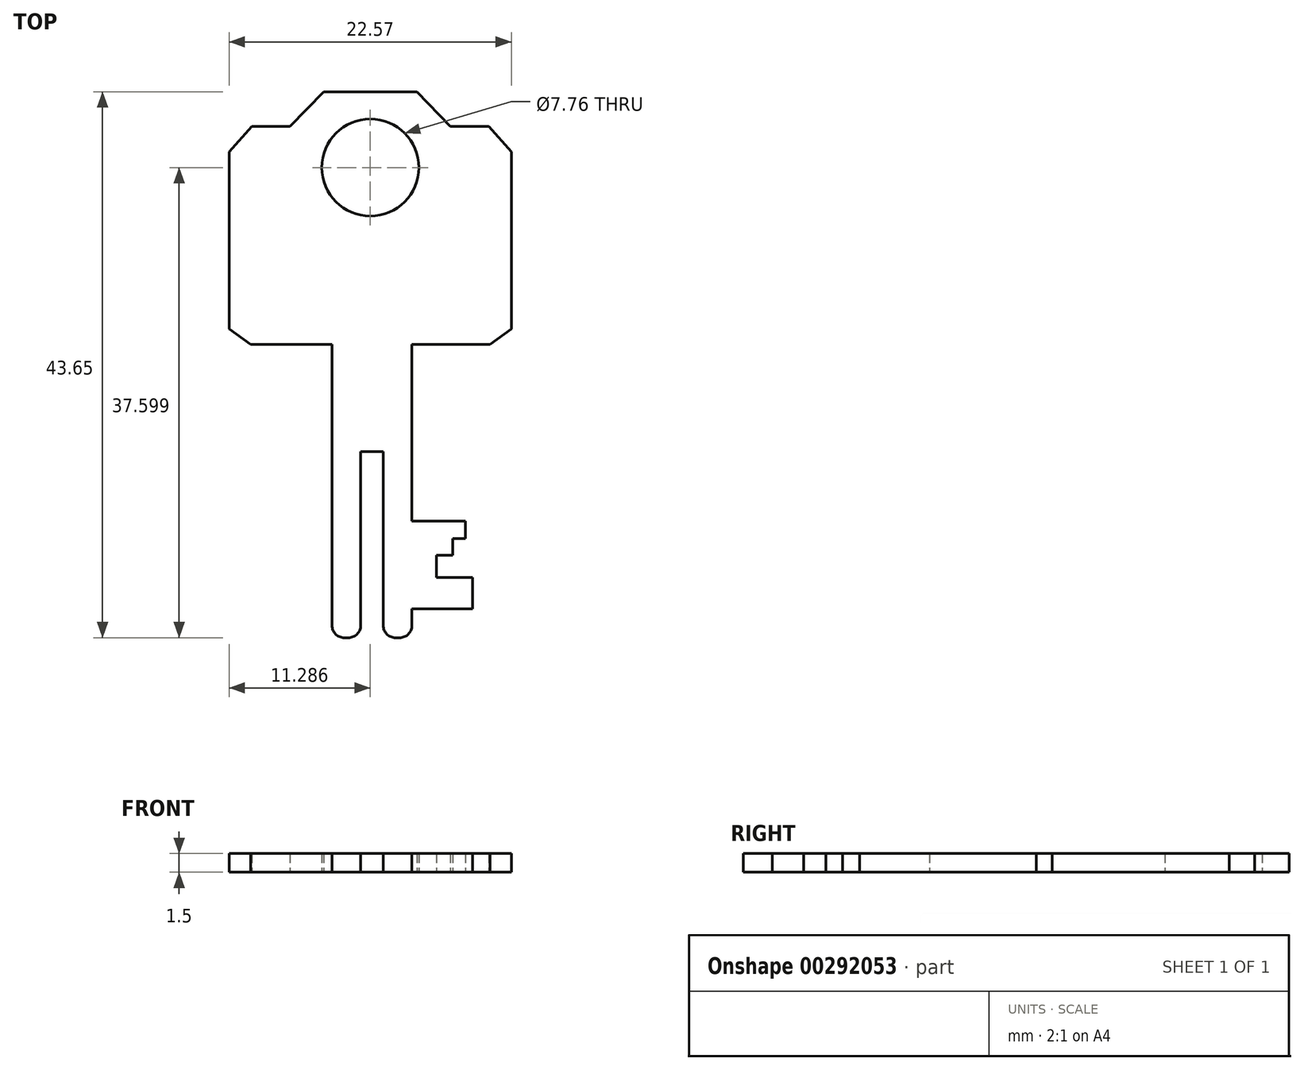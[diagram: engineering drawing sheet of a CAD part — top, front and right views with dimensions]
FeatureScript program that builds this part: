
annotation { "Feature Type Name" : "Feature", "Feature Type Description" : "" }
export const myFeature = defineFeature(function(context is Context, id is Id, definition is map)
    precondition{}
    {
        {
            var Q0;
            Q0=qCreatedBy(makeId("Top.planeOp"),FACE);
            var sketch = newSketch(context, id + "F0", { "sketchPlane" : qUnion([Q0])});
            skLineSegment(sketch, "E0", {"start": v(-40.44, -25.58) * mm, "end": v(-40.44, -51.76) * mm});
            skLineSegment(sketch, "E1", {"start": v(-40.44, -51.76) * mm, "end": v(-38.14, -51.76) * mm});
            skLineSegment(sketch, "E2", {"start": v(-38.14, -51.76) * mm, "end": v(-38.14, -36.87) * mm});
            skLineSegment(sketch, "E3", {"start": v(-38.14, -36.87) * mm, "end": v(-36.34, -36.87) * mm});
            skLineSegment(sketch, "E4", {"start": v(-36.34, -36.87) * mm, "end": v(-36.34, -51.76) * mm});
            skLineSegment(sketch, "E5", {"start": v(-36.34, -51.76) * mm, "end": v(-34.04, -51.76) * mm});
            skLineSegment(sketch, "E6", {"start": v(-34.04, -51.76) * mm, "end": v(-34.04, -49.44) * mm});
            skLineSegment(sketch, "E7", {"start": v(-34.04, -49.44) * mm, "end": v(-29.2, -49.44) * mm});
            skLineSegment(sketch, "E8", {"start": v(-29.2, -49.44) * mm, "end": v(-29.2, -46.94) * mm});
            skLineSegment(sketch, "E9", {"start": v(-29.2, -46.94) * mm, "end": v(-32.07, -46.94) * mm});
            skLineSegment(sketch, "E10", {"start": v(-32.07, -46.94) * mm, "end": v(-32.07, -45.17) * mm});
            skLineSegment(sketch, "E11", {"start": v(-32.07, -45.17) * mm, "end": v(-30.8, -45.17) * mm});
            skLineSegment(sketch, "E12", {"start": v(-30.8, -45.17) * mm, "end": v(-30.8, -43.83) * mm});
            skLineSegment(sketch, "E13", {"start": v(-30.8, -43.83) * mm, "end": v(-29.78, -43.83) * mm});
            skLineSegment(sketch, "E14", {"start": v(-29.78, -43.83) * mm, "end": v(-29.78, -42.44) * mm});
            skLineSegment(sketch, "E15", {"start": v(-29.78, -42.44) * mm, "end": v(-34.04, -42.44) * mm});
            skLineSegment(sketch, "E16", {"start": v(-34.04, -42.44) * mm, "end": v(-34.04, -25.58) * mm});
            skLineSegment(sketch, "E17", {"start": v(-37.37, -28.32) * mm, "end": v(-27.8, -28.32) * mm});
            skLineSegment(sketch, "E18", {"start": v(-26.09, -27.06) * mm, "end": v(-27.8, -28.32) * mm});
            skLineSegment(sketch, "E19", {"start": v(-26.09, -27.06) * mm, "end": v(-26.09, -12.9) * mm});
            skLineSegment(sketch, "E20", {"start": v(-26.09, -12.9) * mm, "end": v(-27.9, -10.86) * mm});
            skLineSegment(sketch, "E21", {"start": v(-27.9, -10.86) * mm, "end": v(-30.96, -10.86) * mm});
            skLineSegment(sketch, "E22", {"start": v(-30.96, -10.86) * mm, "end": v(-33.65, -8.1) * mm});
            skLineSegment(sketch, "E23", {"start": v(-33.65, -8.1) * mm, "end": v(-37.37, -8.1) * mm});
            skLineSegment(sketch, "E24", {"start": v(-37.37, -3.99) * mm, "end": v(-37.37, -56.41) * mm, "construction": true});
            skLineSegment(sketch, "E25.MirrorCS", {"start": v(-41.1, -8.1) * mm, "end": v(-37.37, -8.1) * mm});
            skLineSegment(sketch, "E26.MirrorCS", {"start": v(-43.79, -10.86) * mm, "end": v(-41.1, -8.1) * mm});
            skLineSegment(sketch, "E27.MirrorCS", {"start": v(-46.84, -10.86) * mm, "end": v(-43.79, -10.86) * mm});
            skLineSegment(sketch, "E28.MirrorCS", {"start": v(-48.66, -12.9) * mm, "end": v(-46.84, -10.86) * mm});
            skLineSegment(sketch, "E29.MirrorCS", {"start": v(-48.66, -27.06) * mm, "end": v(-48.66, -12.9) * mm});
            skLineSegment(sketch, "E30.MirrorCS", {"start": v(-48.66, -27.06) * mm, "end": v(-46.94, -28.32) * mm});
            skLineSegment(sketch, "E31.MirrorCS", {"start": v(-37.37, -28.32) * mm, "end": v(-46.94, -28.32) * mm});
            skCircle(sketch, "E32", {"center": v(-37.37, -14.16) * mm, "radius": 3.88 * mm});
            skSolve(sketch);
        }
        {
            var Q0;
            Q0 = qSketchRegion(id + "F0", true);
            extrude(context, id + "F1", {"entities" : qUnion([Q0]), "depth" : 1.5 * mm});
        }
        {
            var Q0;
            Q0=makeQuery(id+"F1.opExtrude","SWEPT_EDGE",EDGE,{"disambiguationData":[OSD([sQuery(id+"F0.wireOp",EDGE,"E1"),sQuery(id+"F0.wireOp",EDGE,"E2")])]});
            var Q1;
            Q1=makeQuery(id+"F1.opExtrude","SWEPT_EDGE",EDGE,{"disambiguationData":[OSD([sQuery(id+"F0.wireOp",EDGE,"E4"),sQuery(id+"F0.wireOp",EDGE,"E5")])]});
            var Q2;
            Q2=makeQuery(id+"F1.opExtrude","SWEPT_EDGE",EDGE,{"disambiguationData":[OSD([sQuery(id+"F0.wireOp",EDGE,"E0"),sQuery(id+"F0.wireOp",EDGE,"E1")])]});
            var Q3;
            Q3=makeQuery(id+"F1.opExtrude","SWEPT_EDGE",EDGE,{"disambiguationData":[OSD([sQuery(id+"F0.wireOp",EDGE,"E5"),sQuery(id+"F0.wireOp",EDGE,"E6")])]});
            fillet(context, id + "F2", {"entities" : qUnion([Q0, Q1, Q2, Q3]), "radius" : 1 * mm, "tangentPropagation" : true, "allowEdgeOverflow" : false});
        }
    });
